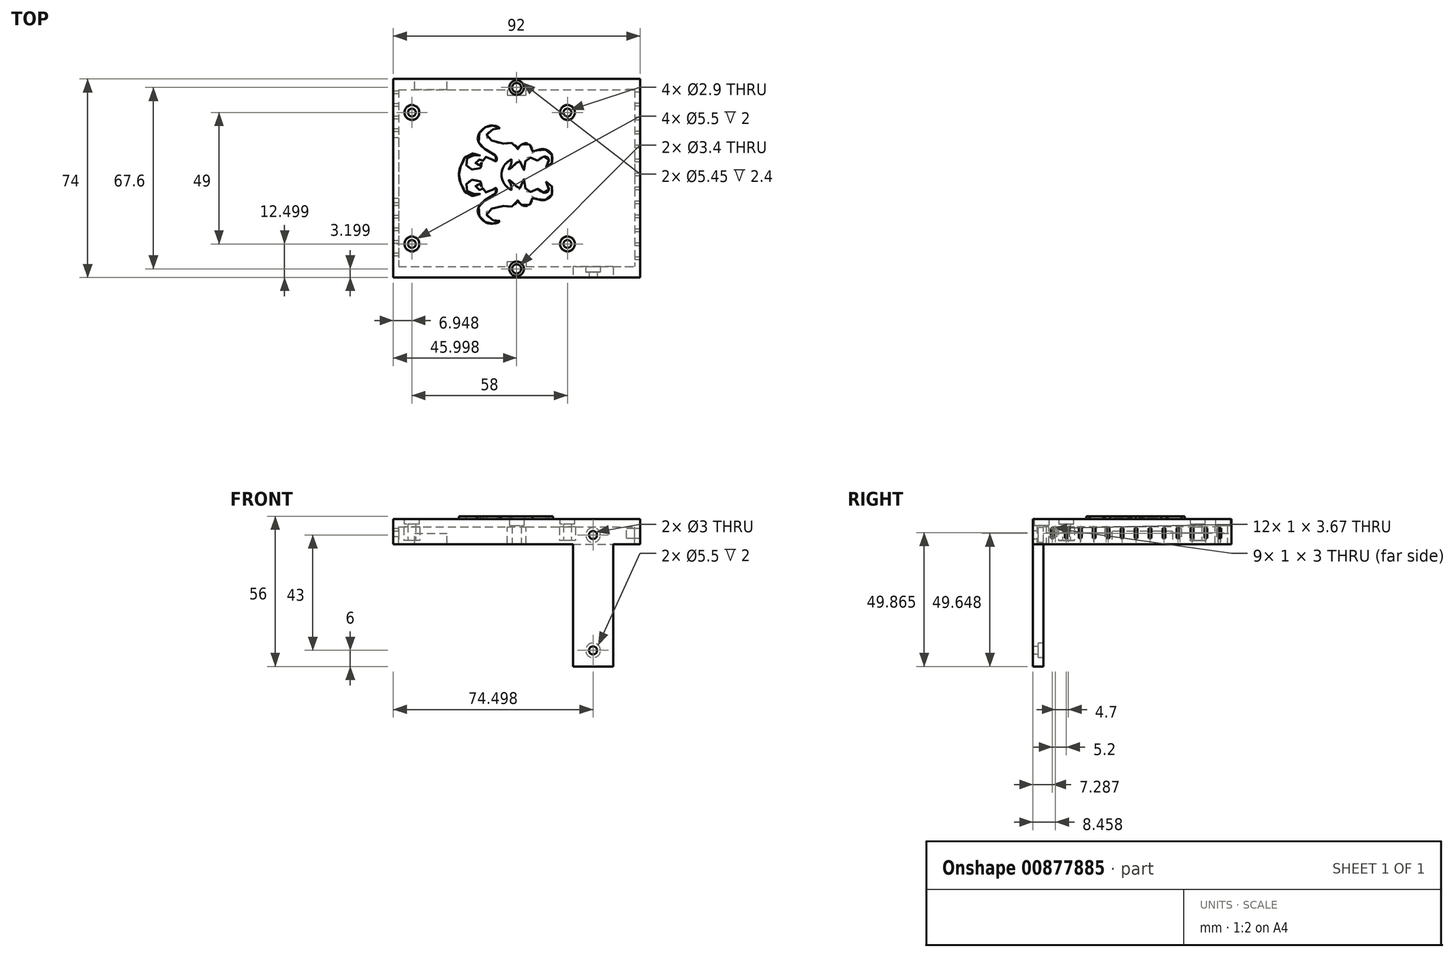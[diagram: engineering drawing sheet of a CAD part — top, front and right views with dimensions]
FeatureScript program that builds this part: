
annotation { "Feature Type Name" : "Feature", "Feature Type Description" : "" }
export const myFeature = defineFeature(function(context is Context, id is Id, definition is map)
    precondition{}
    {
        {
            var Q0;
            Q0=qCreatedBy(makeId("Top.planeOp"),FACE);
            var sketch = newSketch(context, id + "F0", { "sketchPlane" : qUnion([Q0])});
            skCircle(sketch, "E0", {"center": v(-44.94, 22.09) * mm, "radius": 1.45 * mm});
            skCircle(sketch, "E1", {"center": v(-44.94, 22.09) * mm, "radius": 3 * mm});
            skCircle(sketch, "E2", {"center": v(-44.94, -26.91) * mm, "radius": 1.45 * mm});
            skCircle(sketch, "E3", {"center": v(-44.94, -26.91) * mm, "radius": 3 * mm});
            skCircle(sketch, "E4", {"center": v(13.06, -26.91) * mm, "radius": 1.45 * mm});
            skCircle(sketch, "E5", {"center": v(13.06, -26.91) * mm, "radius": 3 * mm});
            skCircle(sketch, "E6", {"center": v(13.06, 22.09) * mm, "radius": 1.45 * mm});
            skCircle(sketch, "E7", {"center": v(13.06, 22.09) * mm, "radius": 3 * mm});
            skPoint(sketch, "E8.middle", {"position": v(-11.6, -2.41) * mm});
            skSolve(sketch);
        }
        {
            var Q0;
            Q0 = qSketchRegion(id + "F0", true);
            extrude(context, id + "F1", {"entities" : qUnion([Q0]), "depth" : 5 * mm, "offsetDistance" : 25 * mm});
        }
        {
            var Q0;
            Q0=makeQuery(id+"F1.opExtrude","CAP_FACE",FACE,{"disambiguationData":[OSD([sQuery(id+"F0.wireOp",EDGE,"E2"),sQuery(id+"F0.wireOp",EDGE,"E3")])],"isStart":false});
            var sketch = newSketch(context, id + "F2", { "sketchPlane" : qUnion([Q0])});
            skLineSegment(sketch, "E9.bottom", {"start": v(-49.9, 30.59) * mm, "end": v(38.1, 30.59) * mm});
            skLineSegment(sketch, "E9.top", {"start": v(-49.9, -35.41) * mm, "end": v(38.1, -35.41) * mm});
            skLineSegment(sketch, "E9.left", {"start": v(-49.9, 30.59) * mm, "end": v(-49.9, -35.41) * mm});
            skLineSegment(sketch, "E9.right", {"start": v(38.1, 30.59) * mm, "end": v(38.1, -35.41) * mm});
            skSolve(sketch);
        }
        {
            var Q0;
            Q0 = qSketchRegion(id + "F2", true);
            extrude(context, id + "F3", {"entities" : qUnion([Q0]), "operationType" : NewBodyOperationType.ADD, "depth" : 3 * mm, "offsetDistance" : 25 * mm});
        }
        {
            var Q0;
            Q0=makeQuery(id+"F0.imprint","IMPRINT",FACE,{"disambiguationData":[TD([[makeQuery(id+"F0.imprint","IMPRINT",EDGE,{"derivedFrom":sQuery(id+"F0.wireOp",EDGE,"E0")}),1.0]])]});
            var Q1;
            Q1=makeQuery(id+"F0.imprint","IMPRINT",FACE,{"disambiguationData":[TD([[makeQuery(id+"F0.imprint","IMPRINT",EDGE,{"derivedFrom":sQuery(id+"F0.wireOp",EDGE,"E2")}),1.0]])]});
            var Q2;
            Q2=makeQuery(id+"F0.imprint","IMPRINT",FACE,{"disambiguationData":[TD([[makeQuery(id+"F0.imprint","IMPRINT",EDGE,{"derivedFrom":sQuery(id+"F0.wireOp",EDGE,"E4")}),1.0]])]});
            var Q3;
            Q3=makeQuery(id+"F0.imprint","IMPRINT",FACE,{"disambiguationData":[TD([[makeQuery(id+"F0.imprint","IMPRINT",EDGE,{"derivedFrom":sQuery(id+"F0.wireOp",EDGE,"E6")}),1.0]])]});
            var Q4;
            Q4=sQuery(id+"F0.wireOp",EDGE,"E6");
            var Q5;
            Q5=sQuery(id+"F0.wireOp",EDGE,"E4");
            var Q6;
            Q6=sQuery(id+"F0.wireOp",EDGE,"E0");
            var Q7;
            Q7=sQuery(id+"F0.wireOp",EDGE,"E2");
            extrude(context, id + "F4", {"entities" : qUnion([Q0, Q1, Q2, Q3]), "operationType" : NewBodyOperationType.REMOVE, "surfaceEntities" : qUnion([Q4, Q5, Q6, Q7]), "depth" : 25 * mm, "offsetDistance" : 25 * mm});
        }
        {
            var Q0;
            Q0=makeQuery(id+"F3.opExtrude","CAP_FACE",FACE,{"disambiguationData":[OSD([sQuery(id+"F2.wireOp",EDGE,"E9.bottom"),sQuery(id+"F2.wireOp",EDGE,"E9.top"),sQuery(id+"F2.wireOp",EDGE,"E9.left"),sQuery(id+"F2.wireOp",EDGE,"E9.right")])],"isStart":false});
            var sketch = newSketch(context, id + "F5", { "sketchPlane" : qUnion([Q0])});
            skCircle(sketch, "E10", {"center": v(-44.94, 22.09) * mm, "radius": 2.75 * mm});
            skCircle(sketch, "E11", {"center": v(-44.94, -26.91) * mm, "radius": 2.75 * mm});
            skCircle(sketch, "E12", {"center": v(13.06, -26.91) * mm, "radius": 2.75 * mm});
            skCircle(sketch, "E13", {"center": v(13.06, 22.09) * mm, "radius": 2.75 * mm});
            skSolve(sketch);
        }
        {
            var Q0;
            Q0 = qSketchRegion(id + "F5", true);
            extrude(context, id + "F6", {"entities" : qUnion([Q0]), "operationType" : NewBodyOperationType.REMOVE, "oppositeDirection" : true, "depth" : 2 * mm, "offsetDistance" : 25 * mm});
        }
        {
            var Q0;
            Q0=makeQuery(id+"F3.opExtrude","CAP_FACE",FACE,{"disambiguationData":[OSD([sQuery(id+"F2.wireOp",EDGE,"E9.bottom"),sQuery(id+"F2.wireOp",EDGE,"E9.top"),sQuery(id+"F2.wireOp",EDGE,"E9.left"),sQuery(id+"F2.wireOp",EDGE,"E9.right")])],"isStart":false});
            var sketch = newSketch(context, id + "F7", { "sketchPlane" : qUnion([Q0])});
            skLineSegment(sketch, "E14.bottom", {"start": v(-49.9, -35.41) * mm, "end": v(38.1, -35.41) * mm});
            skLineSegment(sketch, "E14.top", {"start": v(-49.9, -39.41) * mm, "end": v(38.1, -39.41) * mm});
            skLineSegment(sketch, "E14.left", {"start": v(-49.9, -39.41) * mm, "end": v(-49.9, -35.41) * mm});
            skLineSegment(sketch, "E14.right", {"start": v(38.1, -39.41) * mm, "end": v(38.1, -35.41) * mm});
            skLineSegment(sketch, "E15.bottom", {"start": v(-49.9, -39.41) * mm, "end": v(-51.9, -39.41) * mm});
            skLineSegment(sketch, "E15.top", {"start": v(-49.9, 30.59) * mm, "end": v(-51.9, 30.59) * mm});
            skLineSegment(sketch, "E15.left", {"start": v(-49.9, -39.41) * mm, "end": v(-49.9, 30.59) * mm});
            skLineSegment(sketch, "E15.right", {"start": v(-51.9, -39.41) * mm, "end": v(-51.9, 30.59) * mm});
            skLineSegment(sketch, "E16.bottom", {"start": v(-51.9, 30.59) * mm, "end": v(38.1, 30.59) * mm});
            skLineSegment(sketch, "E16.top", {"start": v(-51.9, 34.59) * mm, "end": v(38.1, 34.59) * mm});
            skLineSegment(sketch, "E16.left", {"start": v(-51.9, 30.59) * mm, "end": v(-51.9, 34.59) * mm});
            skLineSegment(sketch, "E16.right", {"start": v(38.1, 30.59) * mm, "end": v(38.1, 34.59) * mm});
            skLineSegment(sketch, "E17.bottom", {"start": v(38.1, -39.41) * mm, "end": v(40.1, -39.41) * mm});
            skLineSegment(sketch, "E17.top", {"start": v(38.1, 34.59) * mm, "end": v(40.1, 34.59) * mm});
            skLineSegment(sketch, "E17.left", {"start": v(38.1, -39.41) * mm, "end": v(38.1, 34.59) * mm});
            skLineSegment(sketch, "E17.right", {"start": v(40.1, -39.41) * mm, "end": v(40.1, 34.59) * mm});
            skLineSegment(sketch, "E18", {"start": v(-9.4, -35.41) * mm, "end": v(-9.4, -33.41) * mm});
            skLineSegment(sketch, "E19", {"start": v(-9.4, -33.41) * mm, "end": v(-2.4, -33.41) * mm});
            skLineSegment(sketch, "E20", {"start": v(-2.4, -33.41) * mm, "end": v(-2.4, -35.41) * mm});
            skLineSegment(sketch, "E21", {"start": v(-9.4, 30.59) * mm, "end": v(-9.4, 28.59) * mm});
            skLineSegment(sketch, "E22", {"start": v(-9.4, 28.59) * mm, "end": v(-2.4, 28.59) * mm});
            skLineSegment(sketch, "E23", {"start": v(-2.4, 28.59) * mm, "end": v(-2.4, 30.59) * mm});
            skSolve(sketch);
        }
        {
            var Q0;
            Q0=makeQuery(id+"F7.imprint","IMPRINT",FACE,{"disambiguationData":[TD([[makeQuery(id+"F7.imprint","IMPRINT",EDGE,{"derivedFrom":sQuery(id+"F7.wireOp",EDGE,"E14.bottom")}),-1.0]])]});
            var Q1;
            {var subQ5=sQuery(id+"F7.wireOp",EDGE,"E15.bottom");Q1=makeQuery(id+"F7.imprint","IMPRINT",FACE,{"disambiguationData":[TD([[makeQuery(id+"F7.imprint","IMPRINT",EDGE,{"derivedFrom":subQ5}),-1.0]])]});}
            var Q2;
            Q2=makeQuery(id+"F7.imprint","IMPRINT",FACE,{"disambiguationData":[TD([[makeQuery(id+"F7.imprint","IMPRINT",EDGE,{"derivedFrom":sQuery(id+"F7.wireOp",EDGE,"E16.top")}),-1.0]])]});
            var Q3;
            {var subQ3=sQuery(id+"F7.wireOp",EDGE,"E17.bottom");Q3=makeQuery(id+"F7.imprint","IMPRINT",FACE,{"disambiguationData":[TD([[makeQuery(id+"F7.imprint","IMPRINT",EDGE,{"derivedFrom":subQ3}),1.0]])]});}
            var Q4;
            {var subQ0=sQuery(id+"F7.wireOp",EDGE,"E21");Q4=makeQuery(id+"F7.imprint","IMPRINT",FACE,{"disambiguationData":[TD([[makeQuery(id+"F7.imprint","IMPRINT",EDGE,{"derivedFrom":subQ0}),1.0]])]});}
            var Q5;
            {var subQ0=sQuery(id+"F7.wireOp",EDGE,"E18");Q5=makeQuery(id+"F7.imprint","IMPRINT",FACE,{"disambiguationData":[TD([[makeQuery(id+"F7.imprint","IMPRINT",EDGE,{"derivedFrom":subQ0}),-1.0]])]});}
            extrude(context, id + "F8", {"entities" : qUnion([Q0, Q1, Q2, Q3, Q4, Q5]), "operationType" : NewBodyOperationType.ADD, "oppositeDirection" : true, "depth" : 9.4 * mm, "offsetDistance" : 25 * mm});
        }
        {
            var Q0;
            Q0=makeQuery(id+"F8.opExtrude","SWEPT_FACE",FACE,{"disambiguationData":[OSD([sQuery(id+"F7.wireOp",EDGE,"E15.right"),sQuery(id+"F7.wireOp",EDGE,"E16.left")])]});
            var sketch = newSketch(context, id + "F9", { "sketchPlane" : qUnion([Q0])});
            skLineSegment(sketch, "E24.bottom", {"start": v(-12.7, 3.38) * mm, "end": v(9.96, 3.38) * mm});
            skLineSegment(sketch, "E24.top", {"start": v(-12.7, -11.23) * mm, "end": v(9.96, -11.23) * mm});
            skLineSegment(sketch, "E24.left", {"start": v(-12.7, 3.38) * mm, "end": v(-12.7, -11.23) * mm});
            skLineSegment(sketch, "E24.right", {"start": v(9.96, 3.38) * mm, "end": v(9.96, -11.23) * mm});
            skSolve(sketch);
        }
        {
            var Q0;
            Q0 = qSketchRegion(id + "F9", true);
            extrude(context, id + "F10", {"entities" : qUnion([Q0]), "operationType" : NewBodyOperationType.REMOVE, "oppositeDirection" : true, "depth" : 2.9 * mm, "offsetDistance" : 25 * mm});
        }
        {
            var Q0;
            Q0=makeQuery(id+"F8.opExtrude","SWEPT_FACE",FACE,{"disambiguationData":[OSD([sQuery(id+"F7.wireOp",EDGE,"E16.top"),sQuery(id+"F7.wireOp",EDGE,"E17.top")])]});
            var sketch = newSketch(context, id + "F11", { "sketchPlane" : qUnion([Q0])});
            skLineSegment(sketch, "E25.bottom", {"start": v(43.9, -1.4) * mm, "end": v(31.9, -1.4) * mm});
            skLineSegment(sketch, "E25.top", {"start": v(43.9, 2.6) * mm, "end": v(31.9, 2.6) * mm});
            skLineSegment(sketch, "E25.left", {"start": v(43.9, -1.4) * mm, "end": v(43.9, 2.6) * mm});
            skLineSegment(sketch, "E25.right", {"start": v(31.9, -1.4) * mm, "end": v(31.9, 2.6) * mm});
            skSolve(sketch);
        }
        {
            var Q0;
            Q0=makeQuery(id+"F11.imprint","IMPRINT",FACE,{"disambiguationData":[TD([[makeQuery(id+"F11.imprint","IMPRINT",EDGE,{"derivedFrom":sQuery(id+"F11.wireOp",EDGE,"E25.bottom")}),-1.0]])]});
            var Q1;
            {var subQ0=sQuery(id+"F11.wireOp",EDGE,"E25.top");Q1=makeQuery(id+"F11.imprint","IMPRINT",FACE,{"disambiguationData":[TD([[makeQuery(id+"F11.imprint","IMPRINT",EDGE,{"derivedFrom":subQ0}),1.0]])]});}
            extrude(context, id + "F12", {"entities" : qUnion([Q0, Q1]), "operationType" : NewBodyOperationType.REMOVE, "oppositeDirection" : true, "depth" : 5 * mm, "offsetDistance" : 25 * mm});
        }
        {
            var Q0;
            Q0=makeQuery(id+"F8.boolean.opBoolean","MERGE",FACE,{"derivedFrom":[makeQuery(id+"F3.opExtrude","CAP_FACE",FACE,{"disambiguationData":[OSD([sQuery(id+"F2.wireOp",EDGE,"E9.bottom"),sQuery(id+"F2.wireOp",EDGE,"E9.top"),sQuery(id+"F2.wireOp",EDGE,"E9.left"),sQuery(id+"F2.wireOp",EDGE,"E9.right")])],"isStart":false}),makeQuery(id+"F8.opExtrude","CAP_FACE",FACE,{"disambiguationData":[OSD([sQuery(id+"F7.wireOp",EDGE,"E14.bottom"),sQuery(id+"F7.wireOp",EDGE,"E14.top"),sQuery(id+"F7.wireOp",EDGE,"E15.bottom"),sQuery(id+"F7.wireOp",EDGE,"E15.left"),sQuery(id+"F7.wireOp",EDGE,"E15.right"),sQuery(id+"F7.wireOp",EDGE,"E16.bottom"),sQuery(id+"F7.wireOp",EDGE,"E16.top"),sQuery(id+"F7.wireOp",EDGE,"E16.left"),sQuery(id+"F7.wireOp",EDGE,"E17.bottom"),sQuery(id+"F7.wireOp",EDGE,"E17.top"),sQuery(id+"F7.wireOp",EDGE,"E17.left"),sQuery(id+"F7.wireOp",EDGE,"E17.right")])],"isStart":true})]});
            var sketch = newSketch(context, id + "F13", { "sketchPlane" : qUnion([Q0])});
            skFitSpline(sketch, "E26", {"points": [v(11.5, -2.42) * mm, v(12.01, -3.02) * mm, v(12.3, -3.6) * mm, v(12.5, -4.38) * mm, v(12.55, -5.25) * mm, v(12.59, -5.92) * mm, v(12.38, -6.74) * mm, v(12.23, -7.33) * mm, v(11.84, -7.99) * mm, v(11.42, -8.6) * mm, v(10.94, -9.14) * mm, v(10.27, -9.72) * mm, v(9.3, -10.3) * mm, v(8.27, -10.7) * mm, v(7.02, -10.66) * mm, v(6.1, -10.26) * mm, v(5.3, -9.76) * mm, v(4.65, -9.02) * mm, v(3.87, -8.1) * mm, v(3.37, -7.25) * mm, v(1.75, -4.55) * mm, v(1.38, -4.13) * mm, v(1, -3.81) * mm, v(0.52, -3.64) * mm, v(-0.03, -3.53) * mm, v(-0.35, -3.56) * mm, v(-0.73, -3.73) * mm, v(-0.74, -4.08) * mm, v(-0.6, -4.4) * mm, v(0.72, -7.29) * mm, v(1.01, -8.06) * mm, v(1.17, -8.56) * mm, v(0.58, -8.58) * mm, v(0.09, -8.55) * mm, v(-0.55, -8.71) * mm, v(-0.88, -8.73) * mm, v(-0.76, -9.01) * mm, v(-0.45, -9.2) * mm, v(-0.29, -9.45) * mm, v(-0.17, -9.76) * mm, v(-0.09, -10.25) * mm, v(-0.18, -10.56) * mm, v(-0.37, -10.93) * mm, v(-0.64, -11.25) * mm, v(-1.1, -11.5) * mm, v(-1.46, -11.5) * mm, v(-1.75, -11.35) * mm, v(-2, -11.1) * mm, v(-2.23, -10.8) * mm, v(-2.35, -10.36) * mm, v(-2.37, -10.13) * mm, v(-2.35, -9.87) * mm, v(-2.25, -9.58) * mm, v(-1.91, -9.86) * mm, v(-1.6, -9.87) * mm, v(-1.38, -9.71) * mm, v(-1.24, -9.42) * mm, v(-1.3, -9.1) * mm, v(-1.48, -8.86) * mm, v(-1.81, -8.72) * mm, v(-2.1, -8.77) * mm, v(-2.8, -9.25) * mm, v(-3.4, -9.98) * mm, v(-3.74, -10.92) * mm, v(-3.92, -11.77) * mm, v(-3.87, -12.67) * mm, v(-3.67, -13.3) * mm, v(-3.47, -13.79) * mm, v(-3.08, -14.25) * mm, v(-2.6, -14.7) * mm, v(-2.04, -15.03) * mm, v(-1.52, -15.17) * mm, v(-0.88, -15.2) * mm, v(-0.25, -15.01) * mm, v(0.5, -14.5) * mm, v(0.97, -13.86) * mm, v(1.27, -13.22) * mm, v(1.43, -12.62) * mm, v(1.53, -11.96) * mm, v(1.39, -11.1) * mm, v(1.2, -10.53) * mm, v(0.82, -9.84) * mm, v(1.83, -10.1) * mm, v(2.07, -10.85) * mm, v(2.16, -11.43) * mm, v(2.24, -12.24) * mm, v(2.16, -12.95) * mm, v(1.86, -13.9) * mm, v(1.28, -14.86) * mm, v(0.31, -15.7) * mm, v(-0.73, -16.07) * mm, v(-1.94, -16.72) * mm, v(-2.45, -16.99) * mm, v(-2.98, -17.25) * mm, v(-4.03, -17.5) * mm, v(-4.94, -17.64) * mm, v(-5.74, -17.68) * mm], "startDerivative": vector(60.8, -50.95) * mm, "endDerivative": vector(-126.4, 2.27) * mm});
            skFitSpline(sketch, "E27", {"points": [v(11.5, -2.42) * mm, v(11.35, -2.28) * mm, v(11.4, -2.87) * mm, v(11.4, -3.49) * mm, v(11.4, -4.12) * mm, v(11.26, -4.88) * mm, v(10.96, -5.67) * mm, v(10.58, -6.31) * mm, v(10.1, -6.85) * mm, v(9.6, -7.25) * mm, v(9.03, -7.46) * mm, v(8.49, -7.46) * mm, v(7.97, -7.33) * mm, v(7.63, -7.02) * mm, v(7.26, -6.36) * mm, v(6.12, -3.3) * mm, v(5.5, -2.03) * mm, v(5.55, -1.78) * mm, v(5.8, -1.22) * mm, v(6.15, -0.51) * mm, v(6.23, 0.56) * mm, v(6.26, 1.13) * mm, v(6.2, 1.52) * mm, v(6.12, 1.88) * mm, v(6.02, 2.32) * mm, v(5.85, 2.6) * mm, v(5.53, 3) * mm, v(4.95, 3.54) * mm, v(4.41, 3.88) * mm, v(3.76, 4.2) * mm, v(4.27, 4.5) * mm, v(4.72, 4.8) * mm, v(5.05, 5.16) * mm, v(5.51, 5.74) * mm, v(5.72, 6.13) * mm, v(5.88, 6.64) * mm, v(5.95, 7.3) * mm, v(5.81, 8.06) * mm, v(5.52, 8.6) * mm, v(5.1, 9.25) * mm, v(4.71, 9.55) * mm, v(4.3, 9.67) * mm, v(3.68, 9.76) * mm, v(3.15, 9.68) * mm, v(2.75, 9.57) * mm, v(2.3, 9.44) * mm, v(2.6, 10.05) * mm, v(2.97, 10.64) * mm, v(3.24, 11.13) * mm, v(3.46, 11.77) * mm, v(3.64, 12.42) * mm, v(3.75, 12.97) * mm, v(3.74, 13.85) * mm, v(3.56, 14.71) * mm, v(3.28, 15.34) * mm, v(2.97, 15.87) * mm, v(2.63, 16.29) * mm, v(1.9, 16.86) * mm, v(1.3, 17.1) * mm, v(0.85, 17.26) * mm, v(0.29, 17.31) * mm, v(-0.37, 17.26) * mm, v(-1.1, 17.05) * mm, v(-1.66, 16.74) * mm, v(-2.2, 16.3) * mm, v(-2.55, 15.8) * mm, v(-2.84, 15.35) * mm, v(-3.12, 14.8) * mm, v(-2.5, 15.13) * mm, v(-1.82, 15.47) * mm, v(-1.4, 15.62) * mm, v(-0.73, 15.8) * mm, v(-0.3, 15.79) * mm, v(0.18, 15.7) * mm, v(0.43, 15.58) * mm, v(0.7, 15.28) * mm, v(0.92, 14.8) * mm, v(0.98, 14.3) * mm, v(1, 13.85) * mm, v(0.9, 13.28) * mm, v(0.8, 12.76) * mm, v(0.55, 12.4) * mm, v(0.05, 11.92) * mm, v(-0.4, 11.6) * mm, v(-0.62, 11.4) * mm, v(-0.27, 10.92) * mm, v(0.05, 10.35) * mm, v(0.37, 9.68) * mm, v(0.65, 9.02) * mm, v(0.77, 8.4) * mm, v(0.83, 7.9) * mm, v(0.5, 7.53) * mm, v(-0.05, 7.2) * mm, v(-0.65, 7.02) * mm, v(-1.25, 6.92) * mm, v(-1.7, 6.82) * mm, v(-3.4, 6.69) * mm, v(-4.17, 6.69) * mm, v(-3.5, 6.26) * mm, v(-2.75, 5.93) * mm, v(-1.87, 5.46) * mm, v(-1.08, 5.1) * mm, v(-0.39, 4.86) * mm, v(0.16, 4.66) * mm, v(0.4, 4.52) * mm, v(-0.52, 4.12) * mm, v(-1.21, 3.76) * mm, v(-1.93, 3.39) * mm, v(-2.34, 3.04) * mm, v(-2.73, 2.47) * mm, v(-3.1, 1.91) * mm, v(-3.46, 1.43) * mm], "startDerivative": vector(-36.36, 46.62) * mm, "endDerivative": vector(-39.68, -54.25) * mm});
            skFitSpline(sketch, "E28", {"points": [v(-3.46, 1.43) * mm, v(-3.7, 0.84) * mm, v(-3.38, 1.01) * mm, v(-3.13, 1.16) * mm, v(-2.7, 1.34) * mm, v(-2.39, 1.48) * mm, v(-2.04, 1.6) * mm, v(-1.53, 1.73) * mm, v(-1.01, 1.84) * mm, v(-0.72, 1.9) * mm, v(-0.43, 1.92) * mm, v(-0.24, 1.9) * mm, v(-0.08, 1.76) * mm, v(-0.24, 1.43) * mm, v(-0.56, 1) * mm, v(-0.8, 0.67) * mm, v(-1.17, 0.24) * mm, v(-1.5, -0.1) * mm, v(-2.18, -0.71) * mm, v(-2.8, -1.09) * mm, v(-3.46, -1.43) * mm, v(-4.25, -1.68) * mm, v(-4.97, -1.84) * mm, v(-5.74, -1.86) * mm], "startDerivative": vector(-9.4, -16.57) * mm, "endDerivative": vector(-14.48, 0.1) * mm});
            skLineSegment(sketch, "E29", {"start": v(-5.74, -1.86) * mm, "end": v(-5.74, -17.68) * mm});
            skFitSpline(sketch, "E30.MirrorCS", {"points": [v(-8.03, 1.43) * mm, v(-7.77, 0.84) * mm, v(-8.1, 1.01) * mm, v(-8.36, 1.16) * mm, v(-8.79, 1.34) * mm, v(-9.1, 1.48) * mm, v(-9.44, 1.6) * mm, v(-9.95, 1.73) * mm, v(-10.47, 1.84) * mm, v(-10.77, 1.9) * mm, v(-11.06, 1.92) * mm, v(-11.24, 1.9) * mm, v(-11.4, 1.76) * mm, v(-11.25, 1.43) * mm, v(-10.93, 1) * mm, v(-10.7, 0.67) * mm, v(-10.3, 0.24) * mm, v(-10, -0.1) * mm, v(-9.3, -0.71) * mm, v(-8.68, -1.09) * mm, v(-8.03, -1.43) * mm, v(-7.24, -1.68) * mm, v(-6.5, -1.84) * mm, v(-5.74, -1.86) * mm], "startDerivative": vector(9.4, -16.57) * mm, "endDerivative": vector(14.48, 0.1) * mm});
            skFitSpline(sketch, "E31.MirrorCS", {"points": [v(-22.99, -2.42) * mm, v(-23.5, -3.02) * mm, v(-23.79, -3.6) * mm, v(-24, -4.38) * mm, v(-24.04, -5.25) * mm, v(-24.07, -5.92) * mm, v(-23.86, -6.74) * mm, v(-23.72, -7.33) * mm, v(-23.32, -7.99) * mm, v(-22.9, -8.6) * mm, v(-22.42, -9.14) * mm, v(-21.75, -9.72) * mm, v(-20.79, -10.3) * mm, v(-19.75, -10.7) * mm, v(-18.5, -10.66) * mm, v(-17.58, -10.26) * mm, v(-16.79, -9.76) * mm, v(-16.14, -9.02) * mm, v(-15.35, -8.1) * mm, v(-14.86, -7.25) * mm, v(-13.24, -4.55) * mm, v(-12.86, -4.13) * mm, v(-12.5, -3.81) * mm, v(-12, -3.64) * mm, v(-11.45, -3.53) * mm, v(-11.13, -3.56) * mm, v(-10.76, -3.73) * mm, v(-10.74, -4.08) * mm, v(-10.9, -4.4) * mm, v(-12.2, -7.29) * mm, v(-12.5, -8.06) * mm, v(-12.66, -8.56) * mm, v(-12.06, -8.58) * mm, v(-11.57, -8.55) * mm, v(-10.94, -8.71) * mm, v(-10.6, -8.73) * mm, v(-10.72, -9.01) * mm, v(-11.03, -9.2) * mm, v(-11.2, -9.45) * mm, v(-11.3, -9.76) * mm, v(-11.4, -10.25) * mm, v(-11.3, -10.56) * mm, v(-11.12, -10.93) * mm, v(-10.85, -11.25) * mm, v(-10.38, -11.5) * mm, v(-10.02, -11.5) * mm, v(-9.73, -11.35) * mm, v(-9.5, -11.1) * mm, v(-9.25, -10.8) * mm, v(-9.13, -10.36) * mm, v(-9.12, -10.13) * mm, v(-9.14, -9.87) * mm, v(-9.24, -9.58) * mm, v(-9.57, -9.86) * mm, v(-9.88, -9.87) * mm, v(-10.1, -9.71) * mm, v(-10.24, -9.42) * mm, v(-10.19, -9.1) * mm, v(-10, -8.86) * mm, v(-9.67, -8.72) * mm, v(-9.38, -8.77) * mm, v(-8.69, -9.25) * mm, v(-8.08, -9.98) * mm, v(-7.75, -10.92) * mm, v(-7.57, -11.77) * mm, v(-7.62, -12.67) * mm, v(-7.81, -13.3) * mm, v(-8, -13.79) * mm, v(-8.4, -14.25) * mm, v(-8.88, -14.7) * mm, v(-9.44, -15.03) * mm, v(-9.96, -15.17) * mm, v(-10.6, -15.2) * mm, v(-11.24, -15.01) * mm, v(-11.98, -14.5) * mm, v(-12.46, -13.86) * mm, v(-12.76, -13.22) * mm, v(-12.9, -12.62) * mm, v(-13.02, -11.96) * mm, v(-12.87, -11.1) * mm, v(-12.69, -10.53) * mm, v(-12.3, -9.84) * mm, v(-13.31, -10.1) * mm, v(-13.56, -10.85) * mm, v(-13.65, -11.43) * mm, v(-13.73, -12.24) * mm, v(-13.64, -12.95) * mm, v(-13.34, -13.9) * mm, v(-12.77, -14.86) * mm, v(-11.8, -15.7) * mm, v(-10.75, -16.07) * mm, v(-9.54, -16.72) * mm, v(-9.03, -16.99) * mm, v(-8.5, -17.25) * mm, v(-7.45, -17.5) * mm, v(-6.55, -17.64) * mm, v(-5.74, -17.68) * mm], "startDerivative": vector(-60.8, -50.95) * mm, "endDerivative": vector(126.4, 2.27) * mm});
            skFitSpline(sketch, "E32.MirrorCS", {"points": [v(-22.99, -2.42) * mm, v(-22.84, -2.28) * mm, v(-22.88, -2.87) * mm, v(-22.88, -3.49) * mm, v(-22.88, -4.12) * mm, v(-22.75, -4.88) * mm, v(-22.44, -5.67) * mm, v(-22.06, -6.31) * mm, v(-21.58, -6.85) * mm, v(-21.1, -7.25) * mm, v(-20.52, -7.46) * mm, v(-19.97, -7.46) * mm, v(-19.46, -7.33) * mm, v(-19.12, -7.02) * mm, v(-18.74, -6.36) * mm, v(-17.6, -3.3) * mm, v(-16.98, -2.03) * mm, v(-17.04, -1.78) * mm, v(-17.3, -1.22) * mm, v(-17.63, -0.51) * mm, v(-17.72, 0.56) * mm, v(-17.74, 1.13) * mm, v(-17.69, 1.52) * mm, v(-17.6, 1.88) * mm, v(-17.5, 2.32) * mm, v(-17.33, 2.6) * mm, v(-17.01, 3) * mm, v(-16.43, 3.54) * mm, v(-15.9, 3.88) * mm, v(-15.24, 4.2) * mm, v(-15.76, 4.5) * mm, v(-16.2, 4.8) * mm, v(-16.53, 5.16) * mm, v(-17, 5.74) * mm, v(-17.2, 6.13) * mm, v(-17.37, 6.64) * mm, v(-17.43, 7.3) * mm, v(-17.3, 8.06) * mm, v(-17, 8.6) * mm, v(-16.6, 9.25) * mm, v(-16.2, 9.55) * mm, v(-15.8, 9.67) * mm, v(-15.17, 9.76) * mm, v(-14.64, 9.68) * mm, v(-14.23, 9.57) * mm, v(-13.78, 9.44) * mm, v(-14.08, 10.05) * mm, v(-14.46, 10.64) * mm, v(-14.73, 11.13) * mm, v(-14.95, 11.77) * mm, v(-15.12, 12.42) * mm, v(-15.23, 12.97) * mm, v(-15.23, 13.85) * mm, v(-15.05, 14.71) * mm, v(-14.76, 15.34) * mm, v(-14.45, 15.87) * mm, v(-14.12, 16.29) * mm, v(-13.4, 16.86) * mm, v(-12.79, 17.1) * mm, v(-12.34, 17.26) * mm, v(-11.77, 17.31) * mm, v(-11.1, 17.26) * mm, v(-10.38, 17.05) * mm, v(-9.83, 16.74) * mm, v(-9.3, 16.3) * mm, v(-8.94, 15.8) * mm, v(-8.64, 15.35) * mm, v(-8.36, 14.8) * mm, v(-9, 15.13) * mm, v(-9.67, 15.47) * mm, v(-10.1, 15.62) * mm, v(-10.75, 15.8) * mm, v(-11.18, 15.79) * mm, v(-11.67, 15.7) * mm, v(-11.92, 15.58) * mm, v(-12.2, 15.28) * mm, v(-12.4, 14.8) * mm, v(-12.46, 14.3) * mm, v(-12.48, 13.85) * mm, v(-12.38, 13.28) * mm, v(-12.3, 12.76) * mm, v(-12.04, 12.4) * mm, v(-11.54, 11.92) * mm, v(-11.08, 11.6) * mm, v(-10.86, 11.4) * mm, v(-11.21, 10.92) * mm, v(-11.54, 10.35) * mm, v(-11.86, 9.68) * mm, v(-12.13, 9.02) * mm, v(-12.25, 8.4) * mm, v(-12.32, 7.9) * mm, v(-11.98, 7.53) * mm, v(-11.44, 7.2) * mm, v(-10.84, 7.02) * mm, v(-10.23, 6.92) * mm, v(-9.78, 6.82) * mm, v(-8.08, 6.69) * mm, v(-7.31, 6.69) * mm, v(-7.99, 6.26) * mm, v(-8.73, 5.93) * mm, v(-9.61, 5.46) * mm, v(-10.4, 5.1) * mm, v(-11.1, 4.86) * mm, v(-11.65, 4.66) * mm, v(-11.88, 4.52) * mm, v(-10.96, 4.12) * mm, v(-10.27, 3.76) * mm, v(-9.55, 3.39) * mm, v(-9.14, 3.04) * mm, v(-8.76, 2.47) * mm, v(-8.38, 1.91) * mm, v(-8.03, 1.43) * mm], "startDerivative": vector(36.36, 46.62) * mm, "endDerivative": vector(39.68, -54.25) * mm});
            skLineSegment(sketch, "E33", {"start": v(-5.74, -1.86) * mm, "end": v(-5.74, -18.81) * mm, "construction": true});
            skSolve(sketch);
        }
        {
            var Q0;
            Q0 = qSketchRegion(id + "F13", true);
            extrude(context, id + "F14", {"entities" : qUnion([Q0]), "depth" : 1 * mm, "offsetDistance" : 25 * mm});
        }
        {
            var Q0;
            Q0=makeQuery(id+"F14.opExtrude","SWEPT_BODY",BODY,{"disambiguationData":[OSD([sQuery(id+"F13.wireOp",EDGE,"E26"),sQuery(id+"F13.wireOp",EDGE,"E27"),sQuery(id+"F13.wireOp",EDGE,"E28"),sQuery(id+"F13.wireOp",EDGE,"E30.MirrorCS"),sQuery(id+"F13.wireOp",EDGE,"E31.MirrorCS"),sQuery(id+"F13.wireOp",EDGE,"E32.MirrorCS")])]});
            var Q1;
            Q1=makeQuery(id+"F14.opExtrude","SWEPT_EDGE",EDGE,{"disambiguationData":[OSD([sQuery(id+"F13.wireOp",EDGE,"E27"),sQuery(id+"F13.wireOp",EDGE,"E28")])]});
            transform(context, id + "F15", {"entities" : qUnion([Q0]), "transformType" : TransformType.ROTATION, "transformAxis" : qUnion([Q1]), "angle" : 90 * degree, "makeCopy" : false});
        }
        {
            var Q0;
            Q0=makeQuery(id+"F14.opExtrude","SWEPT_BODY",BODY,{"disambiguationData":[OSD([sQuery(id+"F13.wireOp",EDGE,"E26"),sQuery(id+"F13.wireOp",EDGE,"E27"),sQuery(id+"F13.wireOp",EDGE,"E28"),sQuery(id+"F13.wireOp",EDGE,"E30.MirrorCS"),sQuery(id+"F13.wireOp",EDGE,"E31.MirrorCS"),sQuery(id+"F13.wireOp",EDGE,"E32.MirrorCS")])]});
            transform(context, id + "F16", {"entities" : qUnion([Q0]), "transformType" : TransformType.TRANSLATION_3D, "dx" : -4.8 * mm, "dy" : -4.8 * mm, "dz" : 0 * mm, "makeCopy" : false});
        }
        {
            var Q0;
            Q0=makeQuery(id+"F8.opExtrude","SWEPT_FACE",FACE,{"disambiguationData":[OSD([sQuery(id+"F7.wireOp",EDGE,"E17.right")])]});
            var sketch = newSketch(context, id + "F17", { "sketchPlane" : qUnion([Q0])});
            skLineSegment(sketch, "E34.bottom", {"start": v(-32.62, 4.48) * mm, "end": v(-31.62, 4.48) * mm});
            skLineSegment(sketch, "E34.top", {"start": v(-32.62, 0.81) * mm, "end": v(-31.62, 0.81) * mm});
            skLineSegment(sketch, "E34.left", {"start": v(-32.62, 4.48) * mm, "end": v(-32.62, 0.81) * mm});
            skLineSegment(sketch, "E34.right", {"start": v(-31.62, 4.48) * mm, "end": v(-31.62, 0.81) * mm});
            skLineSegment(sketch, "E35.1.0.0", {"start": v(-26.42, 4.48) * mm, "end": v(-26.42, 0.81) * mm});
            skLineSegment(sketch, "E35.1.0.1", {"start": v(-27.42, 4.48) * mm, "end": v(-26.42, 4.48) * mm});
            skLineSegment(sketch, "E35.1.0.2", {"start": v(-27.42, 4.48) * mm, "end": v(-27.42, 0.81) * mm});
            skLineSegment(sketch, "E35.1.0.3", {"start": v(-27.42, 0.81) * mm, "end": v(-26.42, 0.81) * mm});
            skLineSegment(sketch, "E35.2.0.0", {"start": v(-21.22, 4.48) * mm, "end": v(-21.22, 0.81) * mm});
            skLineSegment(sketch, "E35.2.0.1", {"start": v(-22.22, 4.48) * mm, "end": v(-21.22, 4.48) * mm});
            skLineSegment(sketch, "E35.2.0.2", {"start": v(-22.22, 4.48) * mm, "end": v(-22.22, 0.81) * mm});
            skLineSegment(sketch, "E35.2.0.3", {"start": v(-22.22, 0.81) * mm, "end": v(-21.22, 0.81) * mm});
            skLineSegment(sketch, "E35.3.0.0", {"start": v(-16.02, 4.48) * mm, "end": v(-16.02, 0.81) * mm});
            skLineSegment(sketch, "E35.3.0.1", {"start": v(-17.02, 4.48) * mm, "end": v(-16.02, 4.48) * mm});
            skLineSegment(sketch, "E35.3.0.2", {"start": v(-17.02, 4.48) * mm, "end": v(-17.02, 0.81) * mm});
            skLineSegment(sketch, "E35.3.0.3", {"start": v(-17.02, 0.81) * mm, "end": v(-16.02, 0.81) * mm});
            skLineSegment(sketch, "E35.4.0.0", {"start": v(-10.82, 4.48) * mm, "end": v(-10.82, 0.81) * mm});
            skLineSegment(sketch, "E35.4.0.1", {"start": v(-11.82, 4.48) * mm, "end": v(-10.82, 4.48) * mm});
            skLineSegment(sketch, "E35.4.0.2", {"start": v(-11.82, 4.48) * mm, "end": v(-11.82, 0.81) * mm});
            skLineSegment(sketch, "E35.4.0.3", {"start": v(-11.82, 0.81) * mm, "end": v(-10.82, 0.81) * mm});
            skLineSegment(sketch, "E35.5.0.0", {"start": v(-5.62, 4.48) * mm, "end": v(-5.62, 0.81) * mm});
            skLineSegment(sketch, "E35.5.0.1", {"start": v(-6.62, 4.48) * mm, "end": v(-5.62, 4.48) * mm});
            skLineSegment(sketch, "E35.5.0.2", {"start": v(-6.62, 4.48) * mm, "end": v(-6.62, 0.81) * mm});
            skLineSegment(sketch, "E35.5.0.3", {"start": v(-6.62, 0.81) * mm, "end": v(-5.62, 0.81) * mm});
            skLineSegment(sketch, "E35.6.0.0", {"start": v(-0.42, 4.48) * mm, "end": v(-0.42, 0.81) * mm});
            skLineSegment(sketch, "E35.6.0.1", {"start": v(-1.42, 4.48) * mm, "end": v(-0.42, 4.48) * mm});
            skLineSegment(sketch, "E35.6.0.2", {"start": v(-1.42, 4.48) * mm, "end": v(-1.42, 0.81) * mm});
            skLineSegment(sketch, "E35.6.0.3", {"start": v(-1.42, 0.81) * mm, "end": v(-0.42, 0.81) * mm});
            skLineSegment(sketch, "E35.7.0.0", {"start": v(4.78, 4.48) * mm, "end": v(4.78, 0.81) * mm});
            skLineSegment(sketch, "E35.7.0.1", {"start": v(3.78, 4.48) * mm, "end": v(4.78, 4.48) * mm});
            skLineSegment(sketch, "E35.7.0.2", {"start": v(3.78, 4.48) * mm, "end": v(3.78, 0.81) * mm});
            skLineSegment(sketch, "E35.7.0.3", {"start": v(3.78, 0.81) * mm, "end": v(4.78, 0.81) * mm});
            skLineSegment(sketch, "E35.8.0.0", {"start": v(9.98, 4.48) * mm, "end": v(9.98, 0.81) * mm});
            skLineSegment(sketch, "E35.8.0.1", {"start": v(8.98, 4.48) * mm, "end": v(9.98, 4.48) * mm});
            skLineSegment(sketch, "E35.8.0.2", {"start": v(8.98, 4.48) * mm, "end": v(8.98, 0.81) * mm});
            skLineSegment(sketch, "E35.8.0.3", {"start": v(8.98, 0.81) * mm, "end": v(9.98, 0.81) * mm});
            skLineSegment(sketch, "E35.9.0.0", {"start": v(15.18, 4.48) * mm, "end": v(15.18, 0.81) * mm});
            skLineSegment(sketch, "E35.9.0.1", {"start": v(14.18, 4.48) * mm, "end": v(15.18, 4.48) * mm});
            skLineSegment(sketch, "E35.9.0.2", {"start": v(14.18, 4.48) * mm, "end": v(14.18, 0.81) * mm});
            skLineSegment(sketch, "E35.9.0.3", {"start": v(14.18, 0.81) * mm, "end": v(15.18, 0.81) * mm});
            skLineSegment(sketch, "E35.10.0.0", {"start": v(20.38, 4.48) * mm, "end": v(20.38, 0.81) * mm});
            skLineSegment(sketch, "E35.10.0.1", {"start": v(19.38, 4.48) * mm, "end": v(20.38, 4.48) * mm});
            skLineSegment(sketch, "E35.10.0.2", {"start": v(19.38, 4.48) * mm, "end": v(19.38, 0.81) * mm});
            skLineSegment(sketch, "E35.10.0.3", {"start": v(19.38, 0.81) * mm, "end": v(20.38, 0.81) * mm});
            skLineSegment(sketch, "E35.11.0.0", {"start": v(25.58, 4.48) * mm, "end": v(25.58, 0.81) * mm});
            skLineSegment(sketch, "E35.11.0.1", {"start": v(24.58, 4.48) * mm, "end": v(25.58, 4.48) * mm});
            skLineSegment(sketch, "E35.11.0.2", {"start": v(24.58, 4.48) * mm, "end": v(24.58, 0.81) * mm});
            skLineSegment(sketch, "E35.11.0.3", {"start": v(24.58, 0.81) * mm, "end": v(25.58, 0.81) * mm});
            skLineSegment(sketch, "E35.12.0.0", {"start": v(30.78, 4.48) * mm, "end": v(30.78, 0.81) * mm});
            skLineSegment(sketch, "E35.12.0.1", {"start": v(29.78, 4.48) * mm, "end": v(30.78, 4.48) * mm});
            skLineSegment(sketch, "E35.12.0.2", {"start": v(29.78, 4.48) * mm, "end": v(29.78, 0.81) * mm});
            skLineSegment(sketch, "E35.12.0.3", {"start": v(29.78, 0.81) * mm, "end": v(30.78, 0.81) * mm});
            skLineSegment(sketch, "E35.direction1", {"start": v(-31.62, 0.81) * mm, "end": v(-26.42, 0.81) * mm, "construction": true});
            skSolve(sketch);
        }
        {
            var Q0;
            Q0 = qSketchRegion(id + "F17", true);
            extrude(context, id + "F18", {"entities" : qUnion([Q0]), "operationType" : NewBodyOperationType.REMOVE, "oppositeDirection" : true, "depth" : 5 * mm, "offsetDistance" : 25 * mm});
        }
        {
            var Q0;
            Q0=makeQuery(id+"F8.opExtrude","SWEPT_FACE",FACE,{"disambiguationData":[OSD([sQuery(id+"F7.wireOp",EDGE,"E15.right"),sQuery(id+"F7.wireOp",EDGE,"E16.left")])]});
            var sketch = newSketch(context, id + "F19", { "sketchPlane" : qUnion([Q0])});
            skLineSegment(sketch, "E36.bottom", {"start": v(-30.01, 4.37) * mm, "end": v(-29.01, 4.37) * mm});
            skLineSegment(sketch, "E36.top", {"start": v(-30.01, 1.37) * mm, "end": v(-29.01, 1.37) * mm});
            skLineSegment(sketch, "E36.left", {"start": v(-30.01, 4.37) * mm, "end": v(-30.01, 1.37) * mm});
            skLineSegment(sketch, "E36.right", {"start": v(-29.01, 4.37) * mm, "end": v(-29.01, 1.37) * mm});
            skLineSegment(sketch, "E37.1.0.0", {"start": v(-24.31, 4.37) * mm, "end": v(-24.31, 1.37) * mm});
            skLineSegment(sketch, "E37.1.0.1", {"start": v(-25.31, 4.37) * mm, "end": v(-24.31, 4.37) * mm});
            skLineSegment(sketch, "E37.1.0.2", {"start": v(-25.31, 4.37) * mm, "end": v(-25.31, 1.37) * mm});
            skLineSegment(sketch, "E37.1.0.3", {"start": v(-25.31, 1.37) * mm, "end": v(-24.31, 1.37) * mm});
            skLineSegment(sketch, "E37.2.0.0", {"start": v(-19.61, 4.37) * mm, "end": v(-19.61, 1.37) * mm});
            skLineSegment(sketch, "E37.2.0.1", {"start": v(-20.61, 4.37) * mm, "end": v(-19.61, 4.37) * mm});
            skLineSegment(sketch, "E37.2.0.2", {"start": v(-20.61, 4.37) * mm, "end": v(-20.61, 1.37) * mm});
            skLineSegment(sketch, "E37.2.0.3", {"start": v(-20.61, 1.37) * mm, "end": v(-19.61, 1.37) * mm});
            skLineSegment(sketch, "E37.3.0.0", {"start": v(-14.91, 4.37) * mm, "end": v(-14.91, 1.37) * mm});
            skLineSegment(sketch, "E37.3.0.1", {"start": v(-15.91, 4.37) * mm, "end": v(-14.91, 4.37) * mm});
            skLineSegment(sketch, "E37.3.0.2", {"start": v(-15.91, 4.37) * mm, "end": v(-15.91, 1.37) * mm});
            skLineSegment(sketch, "E37.3.0.3", {"start": v(-15.91, 1.37) * mm, "end": v(-14.91, 1.37) * mm});
            skLineSegment(sketch, "E37.direction1", {"start": v(-29.01, 1.37) * mm, "end": v(-24.31, 1.37) * mm, "construction": true});
            skLineSegment(sketch, "E38.bottom", {"start": v(11.65, 4.37) * mm, "end": v(12.65, 4.37) * mm});
            skLineSegment(sketch, "E38.top", {"start": v(11.65, 1.37) * mm, "end": v(12.65, 1.37) * mm});
            skLineSegment(sketch, "E38.left", {"start": v(11.65, 4.37) * mm, "end": v(11.65, 1.37) * mm});
            skLineSegment(sketch, "E38.right", {"start": v(12.65, 4.37) * mm, "end": v(12.65, 1.37) * mm});
            skLineSegment(sketch, "E39.1.0.0", {"start": v(16.35, 4.37) * mm, "end": v(17.35, 4.37) * mm});
            skLineSegment(sketch, "E39.1.0.1", {"start": v(16.35, 4.37) * mm, "end": v(16.35, 1.37) * mm});
            skLineSegment(sketch, "E39.1.0.2", {"start": v(17.35, 4.37) * mm, "end": v(17.35, 1.37) * mm});
            skLineSegment(sketch, "E39.1.0.3", {"start": v(16.35, 1.37) * mm, "end": v(17.35, 1.37) * mm});
            skLineSegment(sketch, "E39.2.0.0", {"start": v(21.05, 4.37) * mm, "end": v(22.05, 4.37) * mm});
            skLineSegment(sketch, "E39.2.0.1", {"start": v(21.05, 4.37) * mm, "end": v(21.05, 1.37) * mm});
            skLineSegment(sketch, "E39.2.0.2", {"start": v(22.05, 4.37) * mm, "end": v(22.05, 1.37) * mm});
            skLineSegment(sketch, "E39.2.0.3", {"start": v(21.05, 1.37) * mm, "end": v(22.05, 1.37) * mm});
            skLineSegment(sketch, "E39.3.0.0", {"start": v(25.75, 4.37) * mm, "end": v(26.75, 4.37) * mm});
            skLineSegment(sketch, "E39.3.0.1", {"start": v(25.75, 4.37) * mm, "end": v(25.75, 1.37) * mm});
            skLineSegment(sketch, "E39.3.0.2", {"start": v(26.75, 4.37) * mm, "end": v(26.75, 1.37) * mm});
            skLineSegment(sketch, "E39.3.0.3", {"start": v(25.75, 1.37) * mm, "end": v(26.75, 1.37) * mm});
            skLineSegment(sketch, "E39.4.0.0", {"start": v(30.45, 4.37) * mm, "end": v(31.45, 4.37) * mm});
            skLineSegment(sketch, "E39.4.0.1", {"start": v(30.45, 4.37) * mm, "end": v(30.45, 1.37) * mm});
            skLineSegment(sketch, "E39.4.0.2", {"start": v(31.45, 4.37) * mm, "end": v(31.45, 1.37) * mm});
            skLineSegment(sketch, "E39.4.0.3", {"start": v(30.45, 1.37) * mm, "end": v(31.45, 1.37) * mm});
            skLineSegment(sketch, "E39.direction1", {"start": v(11.65, 4.37) * mm, "end": v(16.35, 4.37) * mm, "construction": true});
            skSolve(sketch);
        }
        {
            var Q0;
            Q0 = qSketchRegion(id + "F19", true);
            extrude(context, id + "F20", {"entities" : qUnion([Q0]), "operationType" : NewBodyOperationType.REMOVE, "oppositeDirection" : true, "depth" : 2 * mm, "offsetDistance" : 25 * mm});
        }
        {
            var Q0;
            Q0=makeQuery(id+"F8.opExtrude","SWEPT_FACE",FACE,{"disambiguationData":[OSD([sQuery(id+"F7.wireOp",EDGE,"E14.top"),sQuery(id+"F7.wireOp",EDGE,"E15.bottom"),sQuery(id+"F7.wireOp",EDGE,"E17.bottom")])]});
            var sketch = newSketch(context, id + "F21", { "sketchPlane" : qUnion([Q0])});
            skLineSegment(sketch, "E40.bottom", {"start": v(15.1, 8) * mm, "end": v(30.1, 8) * mm});
            skLineSegment(sketch, "E40.top", {"start": v(15.1, -47) * mm, "end": v(30.1, -47) * mm});
            skLineSegment(sketch, "E40.left", {"start": v(15.1, 8) * mm, "end": v(15.1, -47) * mm});
            skLineSegment(sketch, "E40.right", {"start": v(30.1, 8) * mm, "end": v(30.1, -47) * mm});
            skCircle(sketch, "E41", {"center": v(22.6, -41) * mm, "radius": 1.5 * mm});
            skCircle(sketch, "E42", {"center": v(22.6, 2) * mm, "radius": 1.5 * mm});
            skCircle(sketch, "E43", {"center": v(22.6, 2) * mm, "radius": 2.75 * mm});
            skCircle(sketch, "E44", {"center": v(22.6, -41) * mm, "radius": 2.75 * mm});
            skLineSegment(sketch, "E45", {"start": v(22.6, 8) * mm, "end": v(22.6, -47) * mm, "construction": true});
            skSolve(sketch);
        }
        {
            var Q0;
            {var subQ1=sQuery(id+"F21.wireOp",EDGE,"E40.top");Q0=makeQuery(id+"F21.imprint","IMPRINT",FACE,{"disambiguationData":[TD([[makeQuery(id+"F21.imprint","IMPRINT",EDGE,{"derivedFrom":subQ1}),1.0]])]});}
            var Q1;
            {var subQ1=sQuery(id+"F21.wireOp",EDGE,"E40.bottom");Q1=makeQuery(id+"F21.imprint","IMPRINT",FACE,{"disambiguationData":[TD([[makeQuery(id+"F21.imprint","IMPRINT",EDGE,{"derivedFrom":subQ1}),1.0]])]});}
            var Q2;
            Q2=makeQuery(id+"F21.imprint","IMPRINT",FACE,{"disambiguationData":[TD([[makeQuery(id+"F21.imprint","IMPRINT",EDGE,{"derivedFrom":sQuery(id+"F21.wireOp",EDGE,"E41")}),-1.0]])]});
            var Q3;
            {var subQ0=sQuery(id+"F7.wireOp",EDGE,"E14.bottom");Q3=makeQuery(id+"F8.opExtrude","SWEPT_FACE",FACE,{"disambiguationData":[OSD([subQ0]),TDD([makeQuery(id+"F7.imprint","IMPRINT",EDGE,{"disambiguationData":[TD([[makeQuery(id+"F7.imprint","INTERSECT",VERTEX,{"derivedFrom":[subQ0,sQuery(id+"F7.wireOp",EDGE,"E17.left")]}),1.0]])],"derivedFrom":subQ0})])]});}
            extrude(context, id + "F22", {"entities" : qUnion([Q0, Q1, Q2]), "operationType" : NewBodyOperationType.ADD, "endBound" : BoundingType.UP_TO_SURFACE, "oppositeDirection" : true, "depth" : 5 * mm, "endBoundEntityFace" : qUnion([Q3]), "offsetDistance" : 25 * mm});
        }
        {
            var Q0;
            Q0=makeQuery(id+"F21.imprint","IMPRINT",FACE,{"disambiguationData":[TD([[makeQuery(id+"F21.imprint","IMPRINT",EDGE,{"derivedFrom":sQuery(id+"F21.wireOp",EDGE,"E42")}),1.0]])]});
            extrude(context, id + "F23", {"entities" : qUnion([Q0]), "operationType" : NewBodyOperationType.REMOVE, "oppositeDirection" : true, "depth" : 25 * mm, "offsetDistance" : 25 * mm});
        }
        {
            var Q0;
            Q0=makeQuery(id+"F21.imprint","IMPRINT",FACE,{"disambiguationData":[TD([[makeQuery(id+"F21.imprint","IMPRINT",EDGE,{"derivedFrom":sQuery(id+"F21.wireOp",EDGE,"E42")}),-1.0]])]});
            var Q1;
            Q1=makeQuery(id+"F21.imprint","IMPRINT",FACE,{"disambiguationData":[TD([[makeQuery(id+"F21.imprint","IMPRINT",EDGE,{"derivedFrom":sQuery(id+"F21.wireOp",EDGE,"E41")}),-1.0]])]});
            extrude(context, id + "F24", {"entities" : qUnion([Q0, Q1]), "operationType" : NewBodyOperationType.REMOVE, "oppositeDirection" : true, "depth" : 5 * mm, "offsetDistance" : 25 * mm, "hasSecondDirection" : true, "secondDirectionOppositeDirection" : true, "secondDirectionDepth" : 2 * mm});
        }
        {
            var Q0;
            {var subQ1=sQuery(id+"F7.wireOp",EDGE,"E17.right");var subQ3=sQuery(id+"F7.wireOp",EDGE,"E17.left");var subQ5=sQuery(id+"F7.wireOp",EDGE,"E17.top");var subQ6=sQuery(id+"F7.wireOp",EDGE,"E16.top");var subQ8=sQuery(id+"F7.wireOp",EDGE,"E16.bottom");var subQ11=sQuery(id+"F7.wireOp",EDGE,"E14.bottom");var subQ12=makeQuery(id+"F8.opExtrude","SWEPT_FACE",FACE,{"disambiguationData":[OSD([subQ11])]});var subQ13=sQuery(id+"F7.wireOp",EDGE,"E16.left");var subQ14=sQuery(id+"F7.wireOp",EDGE,"E15.right");var subQ16=sQuery(id+"F7.wireOp",EDGE,"E17.bottom");var subQ17=sQuery(id+"F7.wireOp",EDGE,"E15.bottom");var subQ18=sQuery(id+"F7.wireOp",EDGE,"E14.top");var subQ20=sQuery(id+"F7.wireOp",EDGE,"E15.left");Q0=makeQuery(id+"F22.boolean.opBoolean","SPLIT",FACE,{"disambiguationData":[TD([subQ12])],"derivedFrom":makeQuery(id+"F12.boolean.opBoolean","SPLIT",FACE,{"disambiguationData":[TD([subQ12])],"derivedFrom":makeQuery(id+"F8.opExtrude","CAP_FACE",FACE,{"disambiguationData":[OSD([subQ11,subQ18,subQ17,subQ20,subQ14,subQ8,subQ6,subQ13,subQ16,subQ5,subQ3,subQ1])],"isStart":false})})});}
            var sketch = newSketch(context, id + "F25", { "sketchPlane" : qUnion([Q0])});
            skLineSegment(sketch, "E46", {"start": v(-5.9, 39.41) * mm, "end": v(-5.9, -41.09) * mm, "construction": true});
            skCircle(sketch, "E47", {"center": v(-5.9, 36.21) * mm, "radius": 1.7 * mm});
            skCircle(sketch, "E48", {"center": v(-5.9, -31.39) * mm, "radius": 1.7 * mm});
            skCircle(sketch, "E49", {"center": v(-5.9, -31.39) * mm, "radius": 2.73 * mm});
            skCircle(sketch, "E50", {"center": v(-5.9, 36.21) * mm, "radius": 2.73 * mm});
            skSolve(sketch);
        }
        {
            var Q0;
            Q0=makeQuery(id+"F25.imprint","IMPRINT",FACE,{"disambiguationData":[TD([[makeQuery(id+"F25.imprint","IMPRINT",EDGE,{"derivedFrom":sQuery(id+"F25.wireOp",EDGE,"E47")}),1.0]])]});
            var Q1;
            Q1=makeQuery(id+"F25.imprint","IMPRINT",FACE,{"disambiguationData":[TD([[makeQuery(id+"F25.imprint","IMPRINT",EDGE,{"derivedFrom":sQuery(id+"F25.wireOp",EDGE,"E48")}),1.0]])]});
            extrude(context, id + "F26", {"entities" : qUnion([Q0, Q1]), "operationType" : NewBodyOperationType.REMOVE, "oppositeDirection" : true, "depth" : 25 * mm, "offsetDistance" : 25 * mm});
        }
        {
            var Q0;
            {var subQ0=sQuery(id+"F25.wireOp",EDGE,"E50");var subQ1=makeQuery(id+"F8.opExtrude","CAP_EDGE",EDGE,{"disambiguationData":[OSD([sQuery(id+"F7.wireOp",EDGE,"E14.top"),sQuery(id+"F7.wireOp",EDGE,"E15.bottom"),sQuery(id+"F7.wireOp",EDGE,"E17.bottom")])],"isStart":false});var subQ2=makeQuery(id+"F25.imprint","INTERSECT",VERTEX,{"disambiguationData":[OD(0.0)],"derivedFrom":[subQ1,subQ0]});Q0=makeQuery(id+"F25.imprint","IMPRINT",FACE,{"disambiguationData":[TD([[makeQuery(id+"F25.imprint","IMPRINT",EDGE,{"disambiguationData":[TD([[subQ2,1.0]])],"derivedFrom":subQ0}),1.0]])]});}
            var Q1;
            Q1=makeQuery(id+"F25.imprint","IMPRINT",FACE,{"disambiguationData":[TD([[makeQuery(id+"F25.imprint","IMPRINT",EDGE,{"derivedFrom":sQuery(id+"F25.wireOp",EDGE,"E47")}),-1.0]])]});
            var Q2;
            {var subQ0=sQuery(id+"F25.wireOp",EDGE,"E50");var subQ1=makeQuery(id+"F8.opExtrude","CAP_EDGE",EDGE,{"disambiguationData":[OSD([sQuery(id+"F7.wireOp",EDGE,"E14.bottom")])],"isStart":false});var subQ2=makeQuery(id+"F25.imprint","INTERSECT",VERTEX,{"disambiguationData":[OD(0.0)],"derivedFrom":[subQ1,subQ0]});Q2=makeQuery(id+"F25.imprint","IMPRINT",FACE,{"disambiguationData":[TD([[makeQuery(id+"F25.imprint","IMPRINT",EDGE,{"disambiguationData":[TD([[subQ2,-1.0]])],"derivedFrom":subQ0}),1.0]])]});}
            var Q3;
            Q3=makeQuery(id+"F25.imprint","IMPRINT",FACE,{"disambiguationData":[TD([[makeQuery(id+"F25.imprint","IMPRINT",EDGE,{"derivedFrom":sQuery(id+"F25.wireOp",EDGE,"E48")}),-1.0]])]});
            extrude(context, id + "F27", {"entities" : qUnion([Q0, Q1, Q2, Q3]), "operationType" : NewBodyOperationType.REMOVE, "oppositeDirection" : true, "depth" : 10 * mm, "offsetDistance" : 25 * mm, "hasSecondDirection" : true, "secondDirectionOppositeDirection" : true, "secondDirectionDepth" : 7 * mm});
        }
    });
